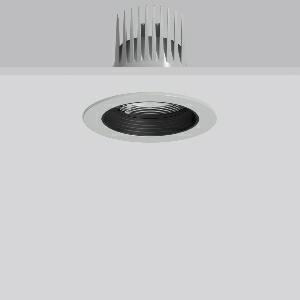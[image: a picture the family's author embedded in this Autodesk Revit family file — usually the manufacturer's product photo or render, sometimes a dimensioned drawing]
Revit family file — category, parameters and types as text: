
# Revit family: heledon_maxi_e_901760_004_3_76_5fb6
name_source: partatom
category: Lighting Fixtures
units: mm (PartAtom-declared; Revit-internal decimal feet)

## family parameters
Cut with Voids When Loaded = No
Host = Face
Light Source = No
Part Type = Normal
Room Calculation Point = No
Round Connector Dimension = Use Diameter
Shared = No

## types (1)
- HELEDON maxi E (1 x LED Modul 935, 2900 lm, 3500)
    Apparent Load = 25 VA
    Approval mark = CE
    CIE Flux Codes = 97 100 100 100 100
    Color Rendering = 92
    Color Temperature = 3500
    Default Elevation = 1800 mm
    Description = Series: HELEDON maxi
Round recessed downlight. Housing: die-cast aluminium, powder-coated. Black plastic ring and recessed LED to prevent glare from the side. Optical assembly with lens made of plastic (polycarbonate) for the best homogeneous light distribution - can be changed without tools. Best colour rendering index Ra>90. Suitable for Recessed ceiling mounting. Installation without tools thanks to spring fastening system. Including separate LED converter with connecting cable 600 mm.High quality converter without flickering and stroboscopic effect. Through-wiring box (5 pole) available as accessory. The following accessories can be mounted without use of tools: interchangeable lenses, decorative glasses, honeycomb louvre, clear and frosted diffusers, white interchangeable plastic ring. 
Colour: silver
Diameter: 162 mm
Height: 3 mm
Cut-out diameter: 152 mm
Recess height: 200 mm
Luminaire: recess height: 135 mm
Lamp: LED
Socket: without socket
Colour temperature: 3500K
Colour rendering index (CRI): 92
System power: 25 W
Rated luminous flux: 2900 lm
Luminous efficiency: 116 lm/W
Control gear: Converter, dimmable, DALI
Protection class: II
Type of protection: IP 20
    Height = 0 mm  [stored 0 ft]
    Lamp = 1 x LED Modul 935
    Lamp Light Flux = 2900 lm
    Lamp count = 1
    Length = 162 mm
    Lifetime = 50000 h
    Luminous efficacy = 116 lm/W
    Manufacturer = RZB
    ModVariant = No
    Model = 901760.004.3.76
    Mounting Place = Ceiling
    Mounting Type = Recessed
    Number of Poles = 1
    OnlyDefault = Yes
    Power Factor = 1
    Product Name = HELEDON maxi E
    Product group = Recessed downlights
    ProductGroupID = 402
    Protection Class = Protection class II
    Protection Degree = IP 20
    RLX_Detail_Level = 1
    RLX_Emergency_Light_Flux = 0 lm
    RLX_Emergency_Type = 0
    RLX_Emergency_Type_DB = No
    RlxData = <blob elided: 119009 chars, md5=249e3f5d>
    Socket = socket
    Standby Power = 0 W
    System Light Flux = 2900 lm
    System Power = 25 W
    Type Comments = Product without accessories
    Type Image = 901663.004.jpg
    URL = http://relux.com
    VarID = ---
    Voltage = 230 V
    Voltage Range = 220-240 V
    Weight = 0.00 kg
    Width = 0 mm  [stored 0 ft]

note: [stored X ft] marks values corroborated as IEEE doubles in the binary element streams (Revit-internal decimal feet)

## geometry (parser evidence)
native form markers: Blend x4, Sweep x11
no freeform markers — native parametric forms only
